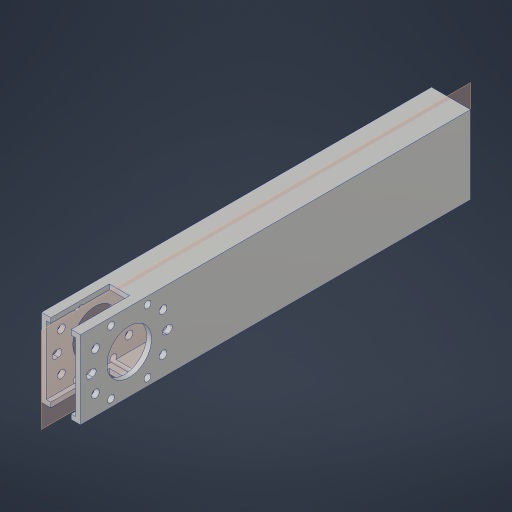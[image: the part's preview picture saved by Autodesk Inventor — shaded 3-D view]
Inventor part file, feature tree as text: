
AUTODESK INVENTOR PART (.ipt)
format: ipt  version: 2023.4 (Build 274418000, 418)  size: 247,296 bytes
history: native  units: in
note: dims shown in document units (in); Inventor stores cm internally (conversion verified against a paired STEP export)
features: hole x3, extrude x2, sketch x2, projected_geometry x1
ambient origin geometry x8: Origin, YZ Plane, XZ Plane, XY Plane, X Axis, Y Axis, Z Axis, Center Point
bodies: Solid1 (feature_tree)
feature tree (8):
  extrude  "Extrusion1"  Depth=1.25in
  sketch  "Sketch2"  dims[d4=0.0in d5=1.25in]
  hole  "Hole1"  [1 undecoded]
  hole  "Hole2"  [1 undecoded]
  hole  "Hole3"  [1 undecoded]
  extrude  "Extrusion2"  Depth=1.0in TaperAngle=360.0deg
  sketch  "Sketch3"  dims[d6=1.14in d7=0.75in d8=0.375in d9=0.25in d10=0.5635in d11=1.0in d12=0.8108in d13=1.875in d14=2.0in d15=4.7244in d17=360.0deg d19=2.3622in d21=360.0deg d23=0.201in d24=0.75in d25=0.332in d26=0.25in d27=0.5635in d28=1.0in d29=0.8108in d30=0.177in d31=0.75in d32=0.385in d33=0.25in d34=0.5635in d35=1.0in d36=0.8108in d37=0.52in d38=1.5in d39=1.0in d40=0.0in]
  projected_geometry  "Project Cut Edges1"
note: 3 required parameter values undecoded (feature->parameter linkage not recoverable at this tier; creation-order binding heuristic only, values carry confidence <= 0.55)
